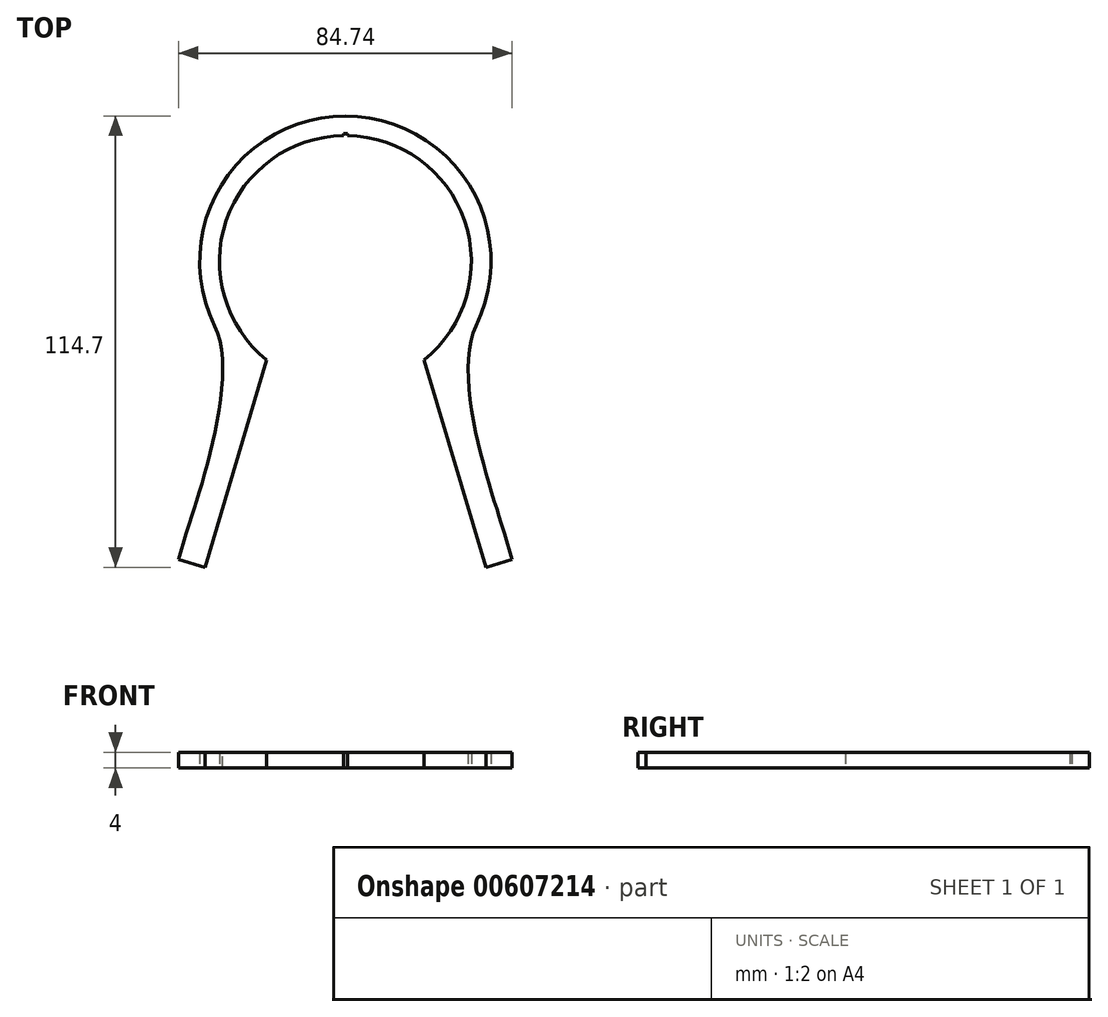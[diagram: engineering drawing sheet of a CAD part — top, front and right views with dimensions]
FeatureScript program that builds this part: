
annotation { "Feature Type Name" : "Feature", "Feature Type Description" : "" }
export const myFeature = defineFeature(function(context is Context, id is Id, definition is map)
    precondition{}
    {
        {
            assignVariable(context, id + "F0", {"name" : "wrenchThickness", "anyValue" : 4});
        }
        {
            var Q0;
            Q0=qCreatedBy(makeId("Top.planeOp"),FACE);
            var sketch = newSketch(context, id + "F1", { "sketchPlane" : qUnion([Q0])});
            skArc(sketch, "E0", {"start": v(33.2, -16.34) * mm, "mid": v(0, 37) * mm, "end": v(-33.2, -16.34) * mm});
            skArc(sketch, "E1", {"start": v(20, -24.98) * mm, "mid": v(0, 32) * mm, "end": v(-20, -24.98) * mm});
            skLineSegment(sketch, "E2", {"start": v(20, -24.98) * mm, "end": v(35.66, -77.7) * mm});
            skLineSegment(sketch, "E3", {"start": v(-20, -24.98) * mm, "end": v(-35.66, -77.7) * mm});
            skLineSegment(sketch, "E4", {"start": v(0, -3.1) * mm, "end": v(0, -86.78) * mm, "construction": true});
            skLineSegment(sketch, "E5", {"start": v(20, -24.98) * mm, "end": v(0, -24.98) * mm, "construction": true});
            skLineSegment(sketch, "E6", {"start": v(0, -24.98) * mm, "end": v(-20, -24.98) * mm, "construction": true});
            skLineSegment(sketch, "E7", {"start": v(-35.66, -77.7) * mm, "end": v(0, -77.7) * mm, "construction": true});
            skLineSegment(sketch, "E8", {"start": v(0, -77.7) * mm, "end": v(35.66, -77.7) * mm, "construction": true});
            skLineSegment(sketch, "E9", {"start": v(-35.66, -77.7) * mm, "end": v(-42.37, -75.7) * mm});
            skLineSegment(sketch, "E10", {"start": v(-42.37, -75.7) * mm, "end": v(-40.41, -69.1) * mm});
            skFitSpline(sketch, "E11", {"points": [v(-40.41, -69.1) * mm, v(-33.2, -16.34) * mm], "startDerivative": vector(7.4, 24.9) * mm, "endDerivative": vector(-19.78, 40.2) * mm});
            skFitSpline(sketch, "E12.MirrorCS", {"points": [v(40.41, -69.1) * mm, v(33.2, -16.34) * mm], "startDerivative": vector(-7.4, 24.9) * mm, "endDerivative": vector(19.78, 40.2) * mm});
            skLineSegment(sketch, "E13.MirrorCS", {"start": v(42.37, -75.7) * mm, "end": v(40.41, -69.1) * mm});
            skLineSegment(sketch, "E14.MirrorCS", {"start": v(35.66, -77.7) * mm, "end": v(42.37, -75.7) * mm});
            skSolve(sketch);
        }
        {
            var Q0;
            Q0=qSketchRegion(id+"F1",true);
            extrude(context, id + "F2", {"entities" : qUnion([Q0]), "depth" : (getVariable(context, 'wrenchThickness')) * mm, "offsetDistance" : 25 * mm});
        }
        {
            var Q0;
            Q0=qCreatedBy(makeId("Top.planeOp"),FACE);
            var sketch = newSketch(context, id + "F3", { "sketchPlane" : qUnion([Q0])});
            skArc(sketch, "E15.0", {"start": v(0.5, 32) * mm, "mid": v(0, 32) * mm, "end": v(-0.5, 32) * mm});
            skLineSegment(sketch, "E16", {"start": v(0, 0) * mm, "end": v(0, 80.2) * mm, "construction": true});
            skLineSegment(sketch, "E17", {"start": v(-0.5, 32) * mm, "end": v(-0.5, 32.5) * mm});
            skLineSegment(sketch, "E18", {"start": v(-0.5, 32.5) * mm, "end": v(0, 32.5) * mm});
            skLineSegment(sketch, "E19", {"start": v(0, 32.5) * mm, "end": v(0.5, 32.5) * mm});
            skLineSegment(sketch, "E20", {"start": v(0.5, 32.5) * mm, "end": v(0.5, 32) * mm});
            skPoint(sketch, "E21.orphan", {"position": v(-20, -24.98) * mm});
            skPoint(sketch, "E22.orphan", {"position": v(20, -24.98) * mm});
            skSolve(sketch);
        }
        {
            var Q0;
            Q0=qSketchRegion(id+"F3",true);
            extrude(context, id + "F4", {"entities" : qUnion([Q0]), "operationType" : NewBodyOperationType.REMOVE, "endBound" : BoundingType.THROUGH_ALL, "depth" : 25 * mm, "offsetDistance" : 25 * mm});
        }
    });
